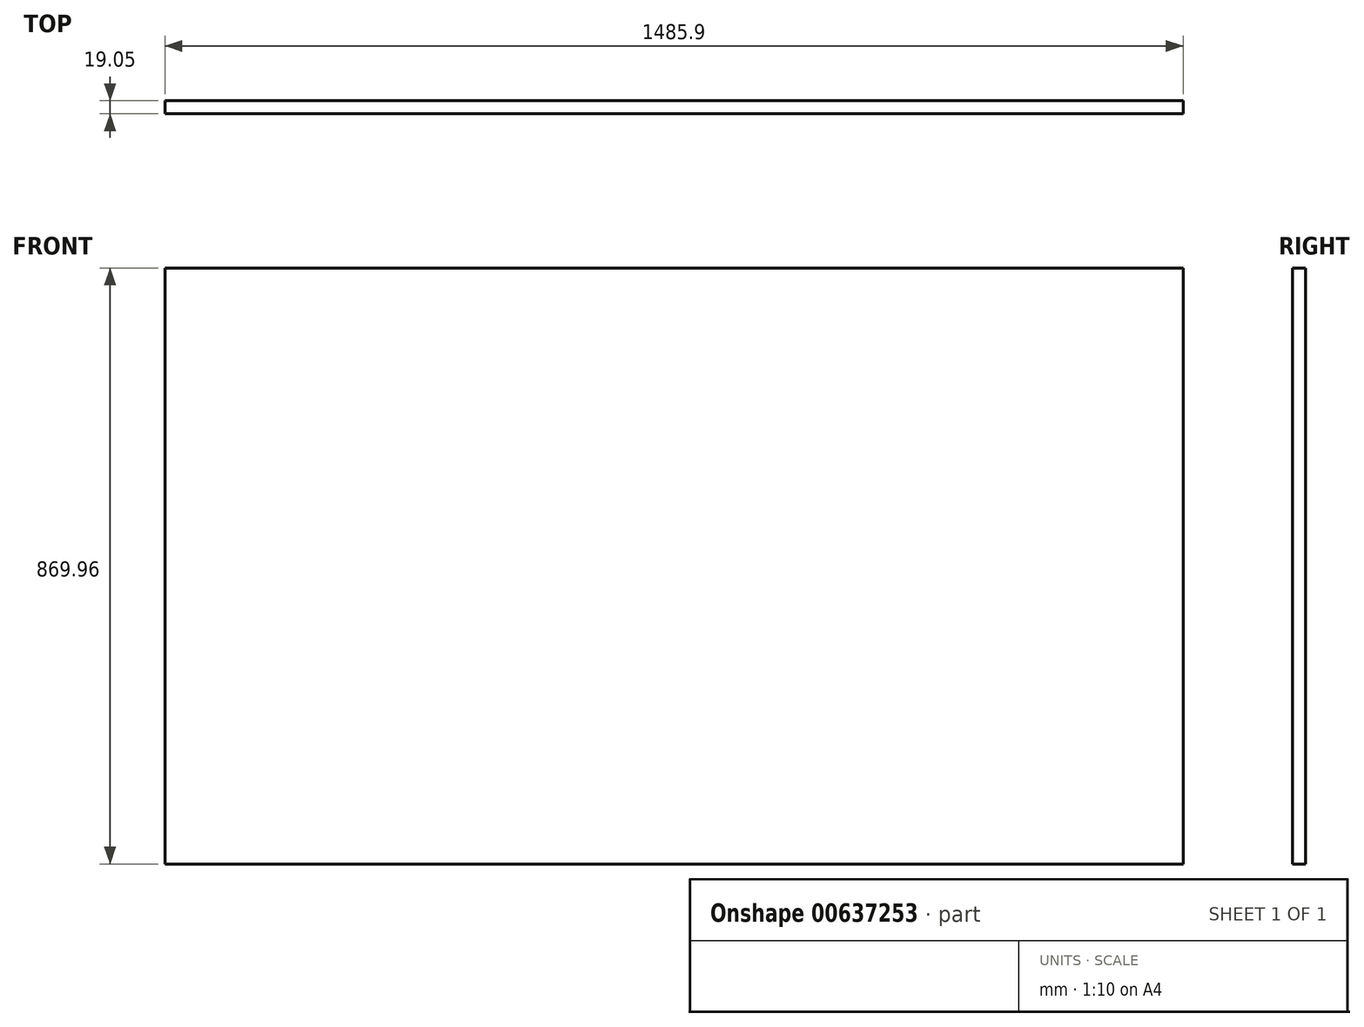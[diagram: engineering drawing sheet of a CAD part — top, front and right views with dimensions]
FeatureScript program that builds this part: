
annotation { "Feature Type Name" : "Feature", "Feature Type Description" : "" }
export const myFeature = defineFeature(function(context is Context, id is Id, definition is map)
    precondition{}
    {
        {
            var Q0;
            Q0=qCreatedBy(makeId("Front.planeOp"),FACE);
            var sketch = newSketch(context, id + "F0", { "sketchPlane" : qUnion([Q0])});
            skLineSegment(sketch, "E0.bottom", {"start": v(-742.95, 434.98) * mm, "end": v(742.95, 434.98) * mm});
            skLineSegment(sketch, "E0.top", {"start": v(-742.95, -434.98) * mm, "end": v(742.95, -434.98) * mm});
            skLineSegment(sketch, "E0.left", {"start": v(-742.95, 434.98) * mm, "end": v(-742.95, -434.98) * mm});
            skLineSegment(sketch, "E0.right", {"start": v(742.95, 434.98) * mm, "end": v(742.95, -434.98) * mm});
            skPoint(sketch, "E0.middle", {"position": v(0, 0) * mm});
            skSolve(sketch);
        }
        {
            var Q0;
            Q0=makeQuery(id+"F0.imprint","IMPRINT",FACE,{"disambiguationData":[TD([[makeQuery(id+"F0.imprint","IMPRINT",EDGE,{"derivedFrom":sQuery(id+"F0.wireOp",EDGE,"E0.bottom")}),-1.0]])]});
            extrude(context, id + "F1", {"entities" : qUnion([Q0]), "depth" : 19.05 * mm, "offsetDistance" : 25.4 * mm});
        }
    });
